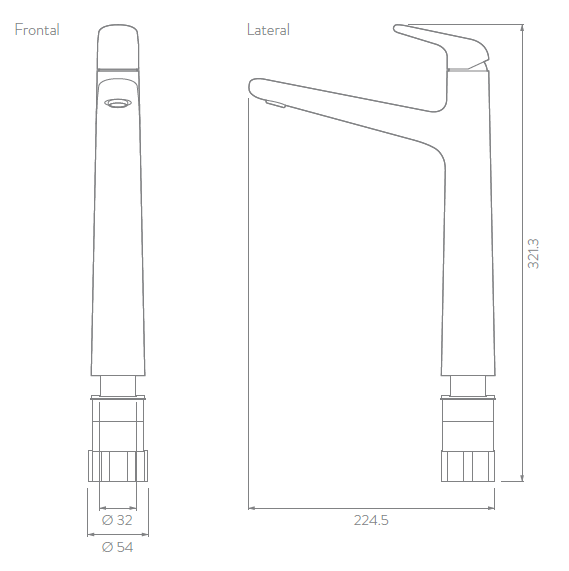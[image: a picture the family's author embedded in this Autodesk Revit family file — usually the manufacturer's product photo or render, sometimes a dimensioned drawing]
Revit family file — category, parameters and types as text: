
# Revit family: LQ1010001_Lavamanos Monocontrol Alto Liquid
name_source: partatom
category: Plumbing Fixtures
units: mm (PartAtom-declared; Revit-internal decimal feet)

## family parameters
Always vertical = Yes
Cut with Voids When Loaded = No
OmniClass Number = 23.31.11.00
OmniClass Title = Faucets
Part Type = Normal
Room Calculation Point = No
Round Connector Dimension = Use Diameter
Shared = No
Work Plane-Based = No

## types (1)
- LQ1010001_Lavamanos Monocontrol Alto Liquid
    Acabado = Corona_Cromado
    Alto = 321 mm  [stored 1.05315 ft]
    Altura de la grifería = Alta
    Ancho = 54 mm  [stored 0.177165 ft]
    Capacidad de flujo = 60 psi: 4,4 L/min
    Colección = Liquid
    Consumo de agua = 5.7 lt
    Creado por = IDD
    Description = La línea de griferías, duchas y accesorios Liquid se inspira en la tensión superficial del agua y en cómo esta crea formas armoniosas adaptándose al ambiente. Al igual que el agua, las superficies de las griferías Liquid juegan con la luz y los reflejos que fluyen alrededorde sus formas, sus líneas continuas y simplicidad formal proporcionan la ventaja práctica y limpieza sin esfuerzo.
Incluye la tecnología Ecostream, de ahorro de agua; y la tecnología ThermoControl, de control más preciso de la temperatura.
Incluye apertura con accionamiento central en frío que evita el encendido automático de calentadores y calderas ahorrando energía; además, es de fácil limpieza gracias al diseño que evita la acumulación de impurezas, es resistente a la corrosión, pelado y decoloración por agua y tiene recubrimientos no tóxicos.
    Fecha de creación = 10/08/2020
    Garantía = 30 años en estructura
    Garantías de otros componentes = 5 años en acabados
    Incluye = Cuerpo, Manija
    Linea = Liquid
    Longitud = 225 mm  [stored 0.738189 ft]
    Material = Metálico
    Peso  Bruto = 2.200 g. - 4,85 lb.
    Peso neto = 2.000 g. - 4,41 lb.
    Presión máxima recomendada = 125 psi (860 Kpa)
    Presión mínima recomendada = 20 psi (140 Kpa)
    Productos compatibles = Lavamanos tipo vessel
    Resistencia = Resistente a la corrosión pelado y decoloración por agua
    Sistema de accionamiento = Palanca monocontrol
    Tecnologías = DuraCrome EcoStream ThermoControl
    Temperaturas máxima de trabajo = 71°C / 159,8°F
    Temperaturas mínima de trabajo = 5°C / 41 °F
    Tipo de Chorro = Espumoso
    Tipo de Grifería = Monocontrol
    Tipo de manija/accionamiento = Palanca
    URL = https://corona.co
    Uso = Residencial
    Vida útil = 500.000 ciclos.

note: [stored X ft] marks values corroborated as IEEE doubles in the binary element streams (Revit-internal decimal feet)

## geometry (parser evidence)
native form markers: Sweep x9
no freeform markers — native parametric forms only
